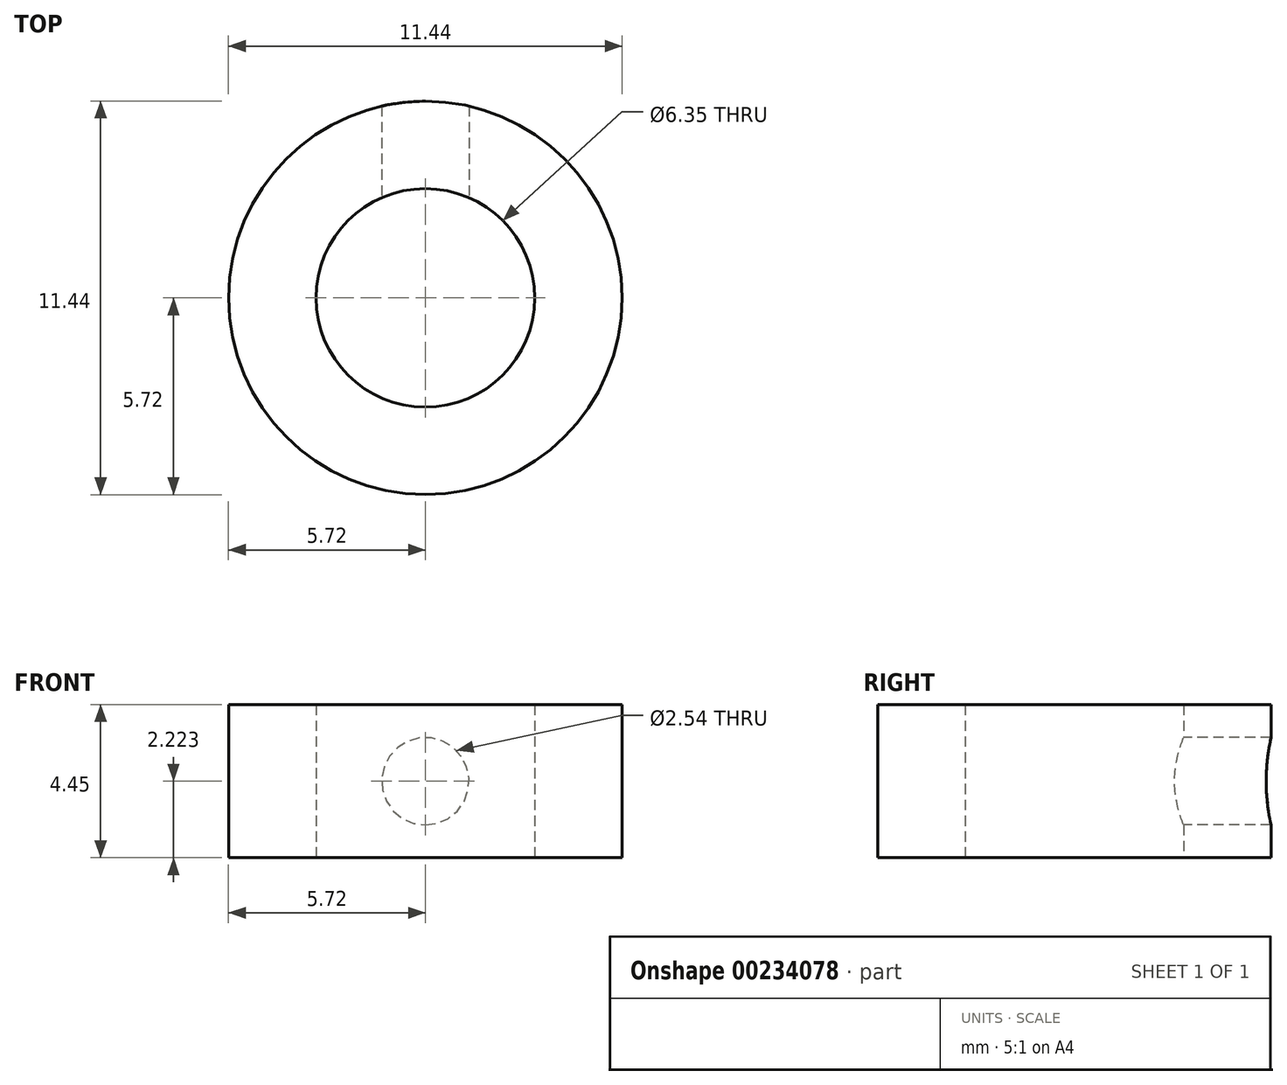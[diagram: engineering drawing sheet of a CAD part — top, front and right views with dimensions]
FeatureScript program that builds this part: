
annotation { "Feature Type Name" : "Feature", "Feature Type Description" : "" }
export const myFeature = defineFeature(function(context is Context, id is Id, definition is map)
    precondition{}
    {
        {
            var Q0;
            Q0=qCreatedBy(makeId("Top.planeOp"),FACE);
            var sketch = newSketch(context, id + "F0", { "sketchPlane" : qUnion([Q0])});
            skCircle(sketch, "E0", {"center": v(0, 0) * mm, "radius": 3.18 * mm});
            skCircle(sketch, "E1", {"center": v(0, 0) * mm, "radius": 5.72 * mm});
            skSolve(sketch);
        }
        {
            var Q0;
            Q0=makeQuery(id+"F0.imprint","IMPRINT",FACE,{"disambiguationData":[TD([[makeQuery(id+"F0.imprint","IMPRINT",EDGE,{"derivedFrom":sQuery(id+"F0.wireOp",EDGE,"E0")}),-1.0]])]});
            extrude(context, id + "F1", {"entities" : qUnion([Q0]), "depth" : 4.44 * mm});
        }
        {
            var Q0;
            Q0=qCreatedBy(makeId("Front.planeOp"),FACE);
            var sketch = newSketch(context, id + "F2", { "sketchPlane" : qUnion([Q0])});
            skLineSegment(sketch, "E2.0", {"start": v(-5.72, 4.45) * mm, "end": v(5.72, 4.45) * mm});
            skLineSegment(sketch, "E3.0", {"start": v(-5.72, 0) * mm, "end": v(5.72, 0) * mm});
            skLineSegment(sketch, "E4", {"start": v(0, 4.45) * mm, "end": v(0, 0) * mm});
            skCircle(sketch, "E5", {"center": v(0, 2.22) * mm, "radius": 1.27 * mm});
            skSolve(sketch);
        }
        {
            var Q0;
            {var subQ0=sQuery(id+"F2.wireOp",EDGE,"E5");var subQ1=sQuery(id+"F2.wireOp",EDGE,"E4");var subQ2=makeQuery(id+"F2.imprint","INTERSECT",VERTEX,{"disambiguationData":[OD(0.0)],"derivedFrom":[subQ1,subQ0]});Q0=makeQuery(id+"F2.imprint","IMPRINT",FACE,{"disambiguationData":[TD([[makeQuery(id+"F2.imprint","IMPRINT",EDGE,{"disambiguationData":[TD([[subQ2,1.0]])],"derivedFrom":subQ1}),1.0]])]});}
            var Q1;
            {var subQ0=sQuery(id+"F2.wireOp",EDGE,"E5");var subQ1=sQuery(id+"F2.wireOp",EDGE,"E4");var subQ2=makeQuery(id+"F2.imprint","INTERSECT",VERTEX,{"disambiguationData":[OD(0.0)],"derivedFrom":[subQ1,subQ0]});Q1=makeQuery(id+"F2.imprint","IMPRINT",FACE,{"disambiguationData":[TD([[makeQuery(id+"F2.imprint","IMPRINT",EDGE,{"disambiguationData":[TD([[subQ2,1.0]])],"derivedFrom":subQ1}),-1.0]])]});}
            extrude(context, id + "F3", {"entities" : qUnion([Q0, Q1]), "operationType" : NewBodyOperationType.REMOVE, "oppositeDirection" : true, "depth" : 25.4 * mm});
        }
    });
